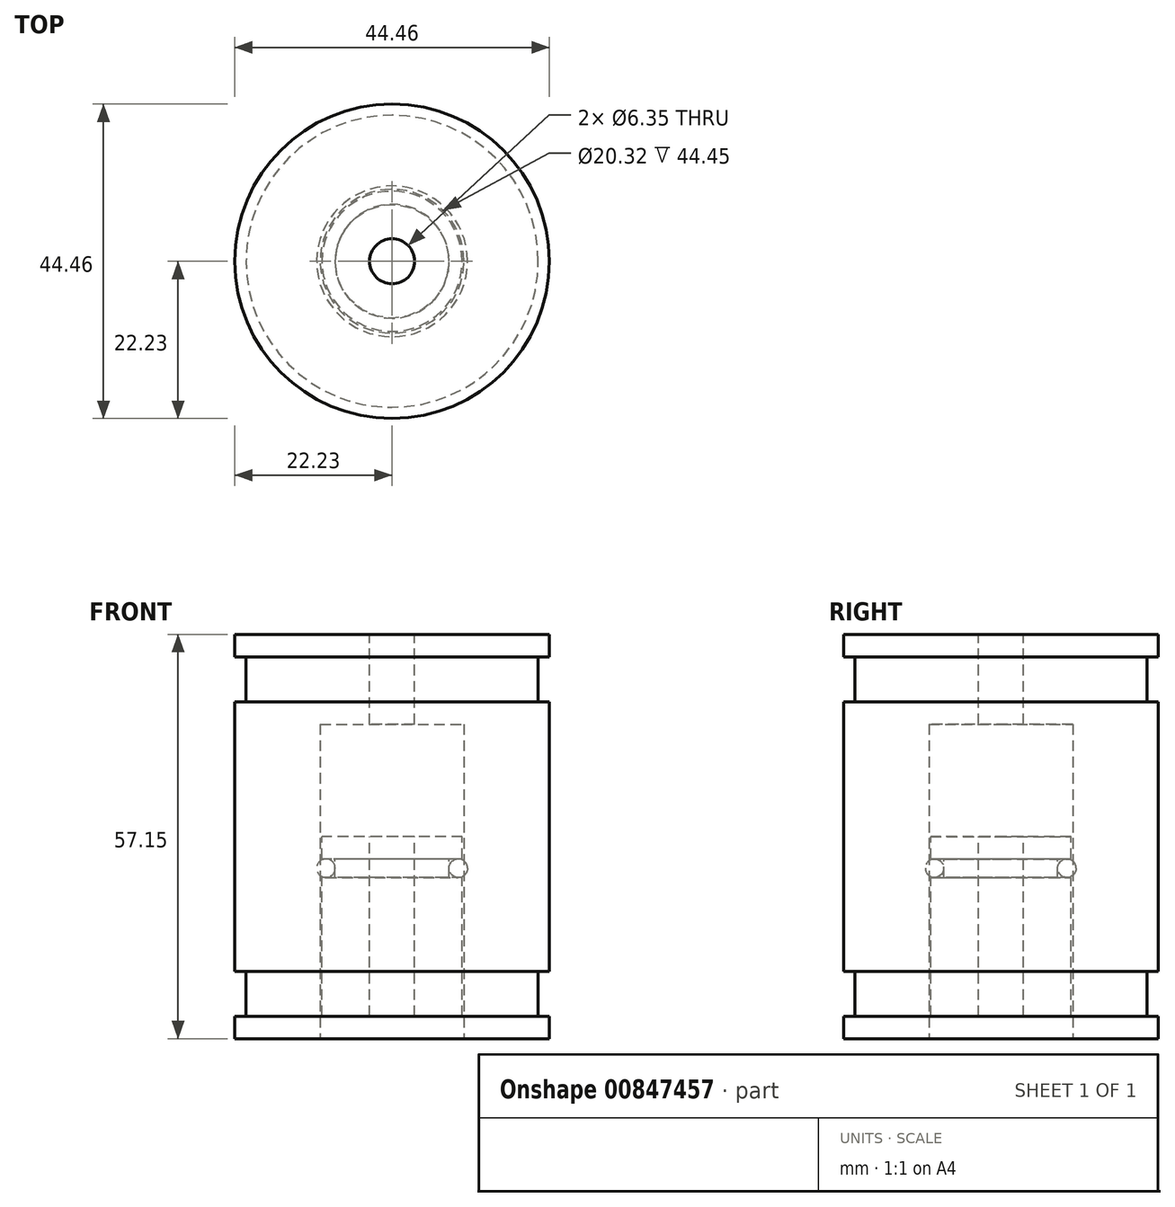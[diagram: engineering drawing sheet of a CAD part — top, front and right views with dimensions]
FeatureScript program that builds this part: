
annotation { "Feature Type Name" : "Feature", "Feature Type Description" : "" }
export const myFeature = defineFeature(function(context is Context, id is Id, definition is map)
    precondition{}
    {
        {
            var Q0;
            Q0=qCreatedBy(makeId("Front.planeOp"),FACE);
            var sketch = newSketch(context, id + "F0", { "sketchPlane" : qUnion([Q0])});
            skLineSegment(sketch, "E0", {"start": v(0, 0) * mm, "end": v(22.23, 0) * mm});
            skLineSegment(sketch, "E1", {"start": v(22.23, 0) * mm, "end": v(22.23, -3.18) * mm});
            skLineSegment(sketch, "E2", {"start": v(22.23, -3.18) * mm, "end": v(20.64, -3.18) * mm});
            skLineSegment(sketch, "E3", {"start": v(20.64, -3.18) * mm, "end": v(20.64, -9.53) * mm});
            skLineSegment(sketch, "E4", {"start": v(20.64, -9.53) * mm, "end": v(22.23, -9.53) * mm});
            skLineSegment(sketch, "E5", {"start": v(22.23, -9.53) * mm, "end": v(22.23, -47.63) * mm});
            skLineSegment(sketch, "E6", {"start": v(22.23, -47.63) * mm, "end": v(20.64, -47.63) * mm});
            skLineSegment(sketch, "E7", {"start": v(20.64, -47.63) * mm, "end": v(20.64, -53.98) * mm});
            skLineSegment(sketch, "E8", {"start": v(20.64, -53.98) * mm, "end": v(22.23, -53.98) * mm});
            skLineSegment(sketch, "E9", {"start": v(22.23, -53.98) * mm, "end": v(22.23, -57.15) * mm});
            skLineSegment(sketch, "E10", {"start": v(22.23, -57.15) * mm, "end": v(10.16, -57.15) * mm});
            skLineSegment(sketch, "E11", {"start": v(10.16, -57.15) * mm, "end": v(10.16, -12.7) * mm});
            skLineSegment(sketch, "E12", {"start": v(10.16, -12.7) * mm, "end": v(0, -12.7) * mm});
            skLineSegment(sketch, "E13", {"start": v(0, -12.7) * mm, "end": v(0, 0) * mm});
            skSolve(sketch);
        }
        {
            var Q0;
            Q0=makeQuery(id+"F0.imprint","IMPRINT",FACE,{"disambiguationData":[TD([[makeQuery(id+"F0.imprint","IMPRINT",EDGE,{"derivedFrom":sQuery(id+"F0.wireOp",EDGE,"E0")}),-1.0]])]});
            var Q1;
            Q1=sQuery(id+"F0.wireOp",EDGE,"E13");
            revolve(context, id + "F1", {"surfaceOperationType" : NewSurfaceOperationType.NEW, "entities" : qUnion([Q0]), "axis" : qUnion([Q1]), "revolveType" : RevolveType.FULL});
        }
        {
            var Q0;
            Q0=qCreatedBy(makeId("Right.planeOp"),FACE);
            var sketch = newSketch(context, id + "F2", { "sketchPlane" : qUnion([Q0])});
            skLineSegment(sketch, "E14.bottom", {"start": v(0, -28.58) * mm, "end": v(9.9, -28.58) * mm});
            skLineSegment(sketch, "E14.top", {"start": v(0, -53.98) * mm, "end": v(9.9, -53.98) * mm});
            skLineSegment(sketch, "E14.left", {"start": v(0, -28.58) * mm, "end": v(0, -53.98) * mm});
            skLineSegment(sketch, "E14.right", {"start": v(9.9, -28.57) * mm, "end": v(9.9, -31.75) * mm});
            skLineSegment(sketch, "E15", {"start": v(9.9, -31.75) * mm, "end": v(8.05, -31.75) * mm});
            skLineSegment(sketch, "E16", {"start": v(8.05, -31.75) * mm, "end": v(8.05, -34.37) * mm});
            skLineSegment(sketch, "E17", {"start": v(8.05, -34.37) * mm, "end": v(9.9, -34.37) * mm});
            skLineSegment(sketch, "E18.trimOffspring", {"start": v(9.9, -34.37) * mm, "end": v(9.9, -53.97) * mm});
            skSolve(sketch);
        }
        {
            var Q0;
            Q0 = qSketchRegion(id + "F2", true);
            var Q1;
            Q1=sQuery(id+"F2.wireOp",EDGE,"E14.left");
            revolve(context, id + "F3", {"surfaceOperationType" : NewSurfaceOperationType.NEW, "entities" : qUnion([Q0]), "axis" : qUnion([Q1]), "revolveType" : RevolveType.FULL});
        }
        {
            var Q0;
            Q0=makeQuery(id+"F1.opRevolve","SWEPT_FACE",FACE,{"disambiguationData":[OSD([sQuery(id+"F0.wireOp",EDGE,"E0")])]});
            var sketch = newSketch(context, id + "F4", { "sketchPlane" : qUnion([Q0])});
            skCircle(sketch, "E19", {"center": v(0, 0) * mm, "radius": 3.18 * mm});
            skSolve(sketch);
        }
        {
            var Q0;
            Q0=makeQuery(id+"F4.imprint","IMPRINT",FACE,{"disambiguationData":[TD([[makeQuery(id+"F4.imprint","IMPRINT",EDGE,{"derivedFrom":sQuery(id+"F4.wireOp",EDGE,"E19")}),1.0]])]});
            extrude(context, id + "F5", {"entities" : qUnion([Q0]), "operationType" : NewBodyOperationType.REMOVE, "endBound" : BoundingType.THROUGH_ALL, "oppositeDirection" : true, "depth" : 25.4 * mm, "offsetDistance" : 25.4 * mm});
        }
        {
            var Q0;
            Q0=qCreatedBy(makeId("Right.planeOp"),FACE);
            var sketch = newSketch(context, id + "F6", { "sketchPlane" : qUnion([Q0])});
            skCircle(sketch, "E20", {"center": v(9.35, -33.06) * mm, "radius": 1.3 * mm});
            skLineSegment(sketch, "E21", {"start": v(9.35, -33.06) * mm, "end": v(10.66, -33.06) * mm, "construction": true});
            skLineSegment(sketch, "E22", {"start": v(8.04, -33.06) * mm, "end": v(0, -33.06) * mm, "construction": true});
            skLineSegment(sketch, "E23", {"start": v(0, -33.06) * mm, "end": v(0, -27.14) * mm, "construction": true});
            skLineSegment(sketch, "E24", {"start": v(9.35, -33.06) * mm, "end": v(9.35, -31.75) * mm, "construction": true});
            skSolve(sketch);
        }
        {
            var Q0;
            Q0 = qSketchRegion(id + "F6", true);
            var Q1;
            Q1=sQuery(id+"F6.wireOp",EDGE,"E23");
            revolve(context, id + "F7", {"surfaceOperationType" : NewSurfaceOperationType.NEW, "entities" : qUnion([Q0]), "axis" : qUnion([Q1]), "revolveType" : RevolveType.FULL});
        }
    });
